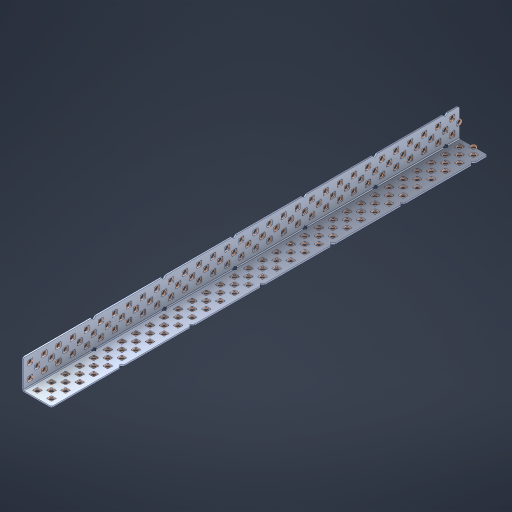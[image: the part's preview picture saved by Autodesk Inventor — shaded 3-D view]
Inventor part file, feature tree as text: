
AUTODESK INVENTOR PART (.ipt)
format: ipt  version: 2023 (Build 270158000, 158)  size: 2,134,016 bytes
history: native  units: in
note: dims shown in document units (in); Inventor stores cm internally (conversion verified against a paired STEP export)
features: other x192, extrude x184, sheet_metal_op x8, sketch x7, pattern_linear x2, mirror x1, chamfer x1
ambient origin geometry x8: Origin, YZ Plane, XZ Plane, XY Plane, X Axis, Y Axis, Z Axis, Center Point
bodies: Solid1 (feature_tree), Body (feature_tree)
feature tree (395):
  sheet_metal_op  "Flanges"
  sheet_metal_op  "Body Pattern"
  pattern_linear  "Center Pattern"  Spacing1=1.0in  [1 undecoded]
  other  "Arc Length"
  pattern_linear  "Notch Pattern"  Spacing1=0.1875in  [1 undecoded]
  other  "Diagonal Plane"
  mirror  "Everything Mirrored"
  chamfer  "End Chamfer"
  sketch  "Sketch1"  dims[d0=1.0in]
  other  "Plate1"
  sketch  "Sketch2"  dims[d1=15.5in]
  other  "Plate2"
  sheet_metal_op  "Bend1"
  sheet_metal_op  "Corner1"
  sketch  "Sketch8"  dims[d2=0.0469in]
  sketch  "Sketch9"  dims[d3=0.0469in]
  other  "Srf91"
  sheet_metal_op  "Body Pattern Sketch"
  other  "Srf92"
  sketch  "Sketch13"  dims[d4=0.0234in]
  sketch  "Sketch15"  dims[d5=0.0938in]
  sketch  "Sketch16"  dims[d6=0.0469in d7=1.0in d8=90.0deg d9=0.0312in d10=0.1875in d11=0.0469in d12=0.0469in d49=0.182in d50=0.02in d52=0.25in d53=0.0469in d54=0.0in d55=0.172in d56=1.0in d57=0.0in d60=12.2047in d62=0.5in d63=0.7874in d65=0.5in d85=0.1473in d86=0.1659in d89=0.0469in d90=0.0in d91=0.04in d92=0.0491in d95=2.5in d96=0.04in d97=0.25in d98=45.0deg d99=0.25in d106=0.182in d107=0.02in d108=0.5in d110=0.0469in d111=0.0in d112=0.172in d113=0.5in d114=0.0in d117=0.5in d123=0.25in d125=0.25in d126=0.0491in d127=0.1227in d128=0.08in d129=0.04in d130=2.5in]
  other  "Srf786"
  other  "Srf856"
  other  "Srf857"
  other  "Srf858"
  other  "Srf859"
  other  "Srf860"
  other  "Srf861"
  other  "Srf889"
  other  "Srf890"
  other  "Srf891"
  other  "Srf1275"
  other  "Srf1276"
  other  "Srf1278"
  other  "Srf1279"
  other  "Srf1280"
  other  "Srf1281"
  other  "Srf1282"
  other  "Srf1283"
  other  "Srf1277"
  other  "Srf1285"
  other  "Srf1286"
  other  "Srf1287"
  other  "Srf1383"
  other  "Srf1384"
  other  "Srf1385"
  other  "Srf1386"
  other  "Srf1387"
  other  "Srf1388"
  other  "Srf1389"
  other  "Srf1390"
  other  "Srf1391"
  other  "Srf1392"
  other  "Srf1393"
  other  "Srf1394"
  other  "Srf1395"
  other  "Srf1396"
  other  "Srf1397"
  other  "Srf1398"
  other  "Srf1399"
  other  "Srf1400"
  other  "Srf1401"
  other  "Srf1402"
  other  "Srf1403"
  other  "Srf1404"
  other  "Srf1405"
  other  "Srf1406"
  other  "Srf1407"
  other  "Srf1408"
  other  "Srf1409"
  other  "Srf1410"
  other  "Srf1411"
  other  "Srf1412"
  other  "Srf1413"
  other  "Srf1414"
  other  "Srf1415"
  other  "Srf1416"
  other  "Srf1417"
  other  "Srf1418"
  other  "Srf1419"
  other  "Srf1420"
  other  "Srf1421"
  other  "Srf1422"
  other  "Srf1423"
  other  "Srf1424"
  other  "Srf1425"
  other  "Srf1426"
  other  "Srf1427"
  other  "Srf1428"
  other  "Srf1429"
  other  "Srf1430"
  other  "Srf1431"
  other  "Srf1432"
  other  "Srf1433"
  other  "Srf1434"
  other  "Srf1435"
  other  "Srf1436"
  other  "Srf1445"
  other  "Srf1446"
  other  "Srf1447"
  other  "Srf1448"
  other  "Srf1449"
  other  "Srf1450"
  other  "Srf1451"
  other  "Srf1452"
  other  "Srf1453"
  other  "Srf1454"
  other  "Srf1455"
  other  "Srf1456"
  other  "Srf1457"
  other  "Srf1458"
  other  "Srf1459"
  other  "Srf1460"
  other  "Srf1461"
  other  "Srf1462"
  other  "Srf1463"
  other  "Srf1464"
  other  "Srf1465"
  other  "Srf1466"
  other  "Srf1467"
  other  "Srf1468"
  other  "Srf1469"
  other  "Srf1470"
  other  "Srf1471"
  other  "Srf1475"
  other  "Srf1476"
  other  "Srf1477"
  other  "Srf1478"
  other  "Srf1479"
  other  "Srf1480"
  other  "Srf1481"
  other  "Srf1482"
  other  "Srf1483"
  other  "Srf1484"
  other  "Srf1485"
  other  "Srf1486"
  other  "Srf1487"
  other  "Srf1488"
  other  "Srf1489"
  other  "Srf1490"
  other  "Srf1491"
  other  "Srf1492"
  other  "Srf1493"
  other  "Srf1494"
  other  "Srf1495"
  other  "Srf1496"
  other  "Srf1497"
  other  "Srf1498"
  other  "Srf1499"
  other  "Srf1500"
  other  "Srf1501"
  other  "Srf1502"
  other  "Srf1503"
  other  "Srf1504"
  other  "Srf1505"
  other  "Srf1506"
  other  "Srf1507"
  other  "Srf1508"
  other  "Srf1509"
  other  "Srf1510"
  other  "Srf1511"
  other  "Srf1512"
  other  "Srf1513"
  other  "Srf1514"
  other  "Srf1515"
  other  "Srf1516"
  other  "Srf1517"
  other  "Srf1518"
  other  "Srf1519"
  other  "Srf1520"
  other  "Srf1521"
  other  "Srf1522"
  other  "Srf1523"
  other  "Srf1524"
  other  "Srf1525"
  other  "Srf1526"
  other  "Srf1527"
  other  "Srf1528"
  other  "Srf1537"
  other  "Srf1538"
  other  "Srf1539"
  other  "Srf1540"
  other  "Srf1541"
  other  "Srf1542"
  other  "Srf1543"
  other  "Srf1544"
  other  "Srf1545"
  other  "Srf1546"
  other  "Srf1547"
  other  "Srf1548"
  other  "Srf1549"
  other  "Srf1550"
  other  "Srf1551"
  other  "Srf1552"
  other  "Srf1553"
  other  "Srf1554"
  other  "Srf1555"
  other  "Srf1556"
  other  "Srf1557"
  other  "Srf1558"
  other  "Srf1559"
  other  "Srf1560"
  other  "Srf1561"
  other  "Srf1562"
  other  "Srf1563"
  sheet_metal_op  "Body Stamp"
  sheet_metal_op  "Body Circle"
  other  "Center Stamp"
  other  "Center Circle"
  sheet_metal_op  "Notch"
  extrude  "ExtrusionSrf92"  Depth=0.0469in
  extrude  "ExtrusionSrf856"  Depth=0.0469in
  extrude  "ExtrusionSrf857"  Depth=0.182in
  extrude  "ExtrusionSrf858"  Depth=0.02in
  extrude  "ExtrusionSrf859"  Depth=0.25in
  extrude  "ExtrusionSrf860"  Depth=0.0469in
  extrude  "ExtrusionSrf861"  TaperAngle=0.0deg  [1 undecoded]
  extrude  "ExtrusionSrf889"  Depth=2.5in
  extrude  "ExtrusionSrf890"  Depth=1.0in TaperAngle=0.0deg
  extrude  "ExtrusionSrf891"  Depth=2.5in
  extrude  "ExtrusionSrf1275"  Depth=0.5in
  extrude  "ExtrusionSrf1276"  Depth=2.5in
  extrude  "ExtrusionSrf1277"  Depth=2.5in
  extrude  "ExtrusionSrf1278"  Depth=0.0469in
  extrude  "ExtrusionSrf1279"  Depth=2.5in TaperAngle=0.0deg
  extrude  "ExtrusionSrf1280"  Depth=2.5in
  extrude  "ExtrusionSrf1281"  Depth=0.25in TaperAngle=45.0deg
  extrude  "ExtrusionSrf1282"  Depth=0.25in
  extrude  "ExtrusionSrf1345"  Depth=0.182in
  extrude  "ExtrusionSrf1346"  Depth=0.02in
  extrude  "ExtrusionSrf1347"  Depth=0.5in
  extrude  "ExtrusionSrf1348"  Depth=0.0469in
  extrude  "ExtrusionSrf1383"  TaperAngle=0.0deg  [1 undecoded]
  extrude  "ExtrusionSrf1384"  Depth=2.5in
  extrude  "ExtrusionSrf1385"  Depth=0.5in TaperAngle=0.0deg
  extrude  "ExtrusionSrf1386"  Depth=0.5in
  extrude  "ExtrusionSrf1387"  Depth=0.25in
  extrude  "ExtrusionSrf1388"  Depth=0.25in
  extrude  "ExtrusionSrf1389"  Depth=2.5in
  extrude  "ExtrusionSrf1390"  Depth=2.5in
  extrude  "ExtrusionSrf1391"  Depth=2.5in
  extrude  "ExtrusionSrf1392"  Depth=2.5in
  extrude  "ExtrusionSrf1393"  Depth=2.5in
  extrude  "ExtrusionSrf1394"  [1 undecoded]
  extrude  "ExtrusionSrf1395"  [1 undecoded]
  extrude  "ExtrusionSrf1396"  [1 undecoded]
  extrude  "ExtrusionSrf1397"  [1 undecoded]
  extrude  "ExtrusionSrf1398"  [1 undecoded]
  extrude  "ExtrusionSrf1399"  [1 undecoded]
  extrude  "ExtrusionSrf1400"  [1 undecoded]
  extrude  "ExtrusionSrf1401"  [1 undecoded]
  extrude  "ExtrusionSrf1402"  [1 undecoded]
  extrude  "ExtrusionSrf1403"  [1 undecoded]
  extrude  "ExtrusionSrf1404"  [1 undecoded]
  extrude  "ExtrusionSrf1405"  [1 undecoded]
  extrude  "ExtrusionSrf1406"  [1 undecoded]
  extrude  "ExtrusionSrf1407"  [1 undecoded]
  extrude  "ExtrusionSrf1408"  [1 undecoded]
  extrude  "ExtrusionSrf1409"  [1 undecoded]
  extrude  "ExtrusionSrf1410"  [1 undecoded]
  extrude  "ExtrusionSrf1411"  [1 undecoded]
  extrude  "ExtrusionSrf1412"  [1 undecoded]
  extrude  "ExtrusionSrf1413"  [1 undecoded]
  extrude  "ExtrusionSrf1414"  [1 undecoded]
  extrude  "ExtrusionSrf1415"  [1 undecoded]
  extrude  "ExtrusionSrf1416"  [1 undecoded]
  extrude  "ExtrusionSrf1417"  [1 undecoded]
  extrude  "ExtrusionSrf1418"  [1 undecoded]
  extrude  "ExtrusionSrf1419"  [1 undecoded]
  extrude  "ExtrusionSrf1420"  [1 undecoded]
  extrude  "ExtrusionSrf1421"  [1 undecoded]
  extrude  "ExtrusionSrf1422"  [1 undecoded]
  extrude  "ExtrusionSrf1423"  [1 undecoded]
  extrude  "ExtrusionSrf1424"  [1 undecoded]
  extrude  "ExtrusionSrf1425"  [1 undecoded]
  extrude  "ExtrusionSrf1426"  [1 undecoded]
  extrude  "ExtrusionSrf1427"  [1 undecoded]
  extrude  "ExtrusionSrf1428"  [1 undecoded]
  extrude  "ExtrusionSrf1429"  [1 undecoded]
  extrude  "ExtrusionSrf1430"  [1 undecoded]
  extrude  "ExtrusionSrf1431"  [1 undecoded]
  extrude  "ExtrusionSrf1432"  [1 undecoded]
  extrude  "ExtrusionSrf1433"  [1 undecoded]
  extrude  "ExtrusionSrf1434"  [1 undecoded]
  extrude  "ExtrusionSrf1435"  [1 undecoded]
  extrude  "ExtrusionSrf1436"  [1 undecoded]
  extrude  "ExtrusionSrf1445"  [1 undecoded]
  extrude  "ExtrusionSrf1446"  [1 undecoded]
  extrude  "ExtrusionSrf1447"  [1 undecoded]
  extrude  "ExtrusionSrf1448"  [1 undecoded]
  extrude  "ExtrusionSrf1449"  [1 undecoded]
  extrude  "ExtrusionSrf1450"  [1 undecoded]
  extrude  "ExtrusionSrf1451"  [1 undecoded]
  extrude  "ExtrusionSrf1452"  [1 undecoded]
  extrude  "ExtrusionSrf1453"  [1 undecoded]
  extrude  "ExtrusionSrf1454"  [1 undecoded]
  extrude  "ExtrusionSrf1455"  [1 undecoded]
  extrude  "ExtrusionSrf1456"  [1 undecoded]
  extrude  "ExtrusionSrf1457"  [1 undecoded]
  extrude  "ExtrusionSrf1458"  [1 undecoded]
  extrude  "ExtrusionSrf1459"  [1 undecoded]
  extrude  "ExtrusionSrf1460"  [1 undecoded]
  extrude  "ExtrusionSrf1461"  [1 undecoded]
  extrude  "ExtrusionSrf1462"  [1 undecoded]
  extrude  "ExtrusionSrf1463"  [1 undecoded]
  extrude  "ExtrusionSrf1464"  [1 undecoded]
  extrude  "ExtrusionSrf1465"  [1 undecoded]
  extrude  "ExtrusionSrf1466"  [1 undecoded]
  extrude  "ExtrusionSrf1467"  [1 undecoded]
  extrude  "ExtrusionSrf1468"  [1 undecoded]
  extrude  "ExtrusionSrf1469"  [1 undecoded]
  extrude  "ExtrusionSrf1470"  [1 undecoded]
  extrude  "ExtrusionSrf1471"  [1 undecoded]
  extrude  "ExtrusionSrf1475"  [1 undecoded]
  extrude  "ExtrusionSrf1476"  [1 undecoded]
  extrude  "ExtrusionSrf1477"  [1 undecoded]
  extrude  "ExtrusionSrf1478"  [1 undecoded]
  extrude  "ExtrusionSrf1479"  [1 undecoded]
  extrude  "ExtrusionSrf1480"  [1 undecoded]
  extrude  "ExtrusionSrf1481"  [1 undecoded]
  extrude  "ExtrusionSrf1482"  [1 undecoded]
  extrude  "ExtrusionSrf1483"  [1 undecoded]
  extrude  "ExtrusionSrf1484"  [1 undecoded]
  extrude  "ExtrusionSrf1485"  [1 undecoded]
  extrude  "ExtrusionSrf1486"  [1 undecoded]
  extrude  "ExtrusionSrf1487"  [1 undecoded]
  extrude  "ExtrusionSrf1488"  [1 undecoded]
  extrude  "ExtrusionSrf1489"  [1 undecoded]
  extrude  "ExtrusionSrf1490"  [1 undecoded]
  extrude  "ExtrusionSrf1491"  [1 undecoded]
  extrude  "ExtrusionSrf1492"  [1 undecoded]
  extrude  "ExtrusionSrf1493"  [1 undecoded]
  extrude  "ExtrusionSrf1494"  [1 undecoded]
  extrude  "ExtrusionSrf1495"  [1 undecoded]
  extrude  "ExtrusionSrf1496"  [1 undecoded]
  extrude  "ExtrusionSrf1497"  [1 undecoded]
  extrude  "ExtrusionSrf1498"  [1 undecoded]
  extrude  "ExtrusionSrf1499"  [1 undecoded]
  extrude  "ExtrusionSrf1500"  [1 undecoded]
  extrude  "ExtrusionSrf1501"  [1 undecoded]
  extrude  "ExtrusionSrf1502"  [1 undecoded]
  extrude  "ExtrusionSrf1503"  [1 undecoded]
  extrude  "ExtrusionSrf1504"  [1 undecoded]
  extrude  "ExtrusionSrf1505"  [1 undecoded]
  extrude  "ExtrusionSrf1506"  [1 undecoded]
  extrude  "ExtrusionSrf1507"  [1 undecoded]
  extrude  "ExtrusionSrf1508"  [1 undecoded]
  extrude  "ExtrusionSrf1509"  [1 undecoded]
  extrude  "ExtrusionSrf1510"  [1 undecoded]
  extrude  "ExtrusionSrf1511"  [1 undecoded]
  extrude  "ExtrusionSrf1512"  [1 undecoded]
  extrude  "ExtrusionSrf1513"  [1 undecoded]
  extrude  "ExtrusionSrf1514"  [1 undecoded]
  extrude  "ExtrusionSrf1515"  [1 undecoded]
  extrude  "ExtrusionSrf1516"  [1 undecoded]
  extrude  "ExtrusionSrf1517"  [1 undecoded]
  extrude  "ExtrusionSrf1518"  [1 undecoded]
  extrude  "ExtrusionSrf1519"  [1 undecoded]
  extrude  "ExtrusionSrf1520"  [1 undecoded]
  extrude  "ExtrusionSrf1521"  [1 undecoded]
  extrude  "ExtrusionSrf1522"  [1 undecoded]
  extrude  "ExtrusionSrf1523"  [1 undecoded]
  extrude  "ExtrusionSrf1524"  [1 undecoded]
  extrude  "ExtrusionSrf1525"  [1 undecoded]
  extrude  "ExtrusionSrf1526"  [1 undecoded]
  extrude  "ExtrusionSrf1527"  [1 undecoded]
  extrude  "ExtrusionSrf1528"  [1 undecoded]
  extrude  "ExtrusionSrf1537"  [1 undecoded]
  extrude  "ExtrusionSrf1538"  [1 undecoded]
  extrude  "ExtrusionSrf1539"  [1 undecoded]
  extrude  "ExtrusionSrf1540"  [1 undecoded]
  extrude  "ExtrusionSrf1541"  [1 undecoded]
  extrude  "ExtrusionSrf1542"  [1 undecoded]
  extrude  "ExtrusionSrf1543"  [1 undecoded]
  extrude  "ExtrusionSrf1544"  [1 undecoded]
  extrude  "ExtrusionSrf1545"  [1 undecoded]
  extrude  "ExtrusionSrf1546"  [1 undecoded]
  extrude  "ExtrusionSrf1547"  [1 undecoded]
  extrude  "ExtrusionSrf1548"  [1 undecoded]
  extrude  "ExtrusionSrf1549"  [1 undecoded]
  extrude  "ExtrusionSrf1550"  [1 undecoded]
  extrude  "ExtrusionSrf1551"  [1 undecoded]
  extrude  "ExtrusionSrf1552"  [1 undecoded]
  extrude  "ExtrusionSrf1553"  [1 undecoded]
  extrude  "ExtrusionSrf1554"  [1 undecoded]
  extrude  "ExtrusionSrf1555"  [1 undecoded]
  extrude  "ExtrusionSrf1556"  [1 undecoded]
  extrude  "ExtrusionSrf1557"  [1 undecoded]
  extrude  "ExtrusionSrf1558"  [1 undecoded]
  extrude  "ExtrusionSrf1559"  [1 undecoded]
  extrude  "ExtrusionSrf1560"  [1 undecoded]
  extrude  "ExtrusionSrf1561"  [1 undecoded]
  extrude  "ExtrusionSrf1562"  [1 undecoded]
  extrude  "ExtrusionSrf1563"  [1 undecoded]
note: 155 required parameter values undecoded (feature->parameter linkage not recoverable at this tier; creation-order binding heuristic only, values carry confidence <= 0.55)
